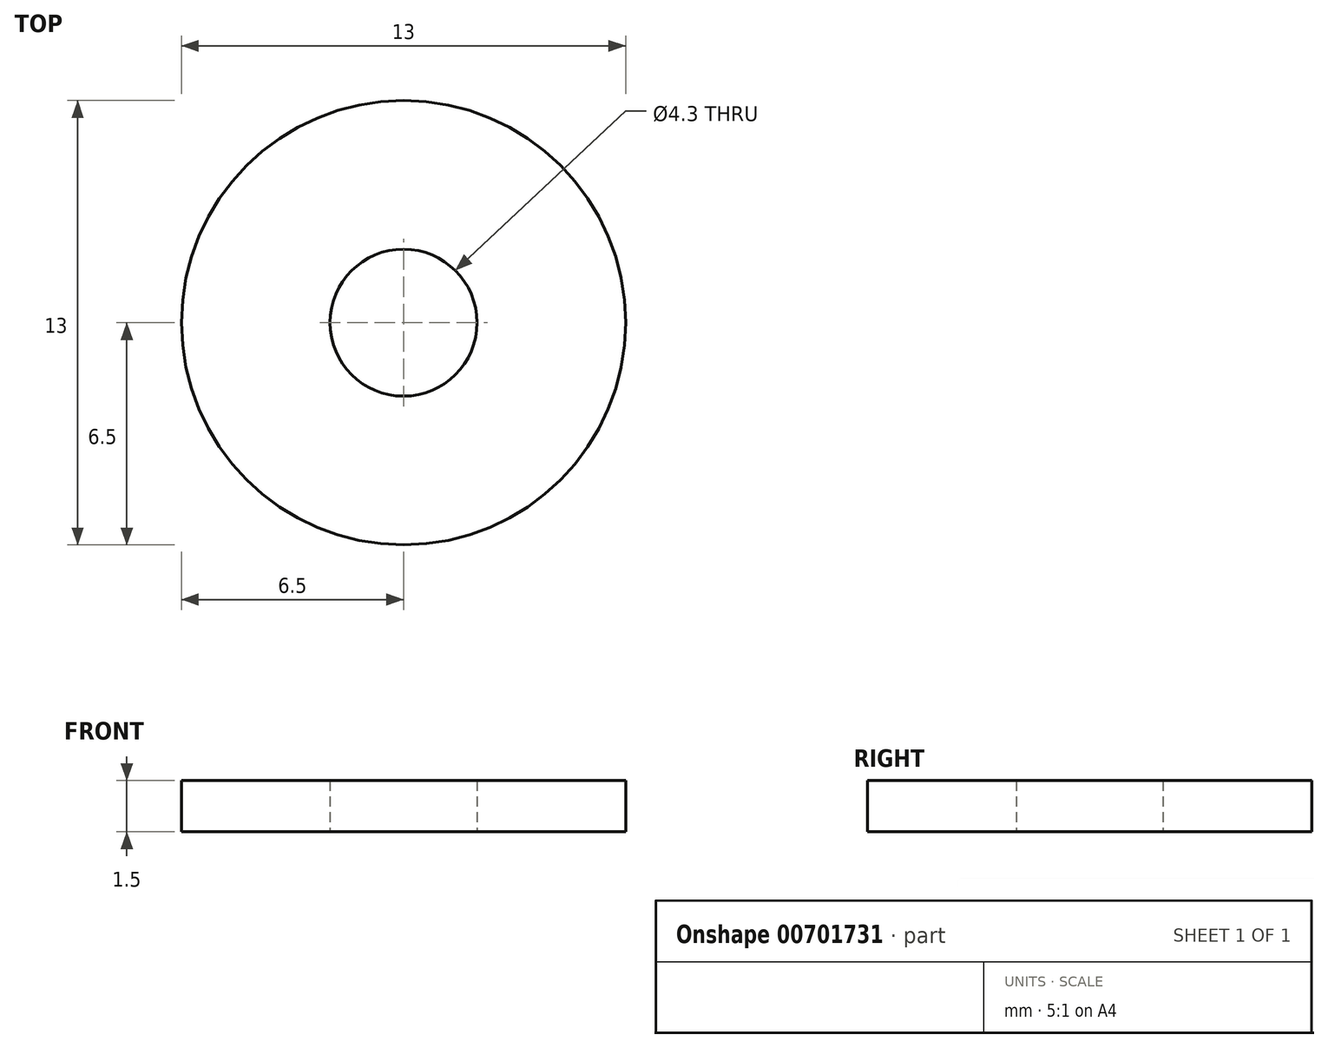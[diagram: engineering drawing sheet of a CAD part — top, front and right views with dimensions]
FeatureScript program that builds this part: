
annotation { "Feature Type Name" : "Feature", "Feature Type Description" : "" }
export const myFeature = defineFeature(function(context is Context, id is Id, definition is map)
    precondition{}
    {
        {
            var Q0;
            Q0=qCreatedBy(makeId("Top.planeOp"),FACE);
            var sketch = newSketch(context, id + "F0", { "sketchPlane" : qUnion([Q0])});
            skCircle(sketch, "E0", {"center": v(0, 0) * mm, "radius": 6.5 * mm});
            skCircle(sketch, "E1", {"center": v(0, 0) * mm, "radius": 2.15 * mm});
            skSolve(sketch);
        }
        {
            var Q0;
            Q0=makeQuery(id+"F0.imprint","IMPRINT",FACE,{"disambiguationData":[TD([[makeQuery(id+"F0.imprint","IMPRINT",EDGE,{"derivedFrom":sQuery(id+"F0.wireOp",EDGE,"E0")}),1.0]])]});
            extrude(context, id + "F1", {"entities" : qUnion([Q0]), "depth" : 1.5 * mm, "offsetDistance" : 25 * mm});
        }
    });
